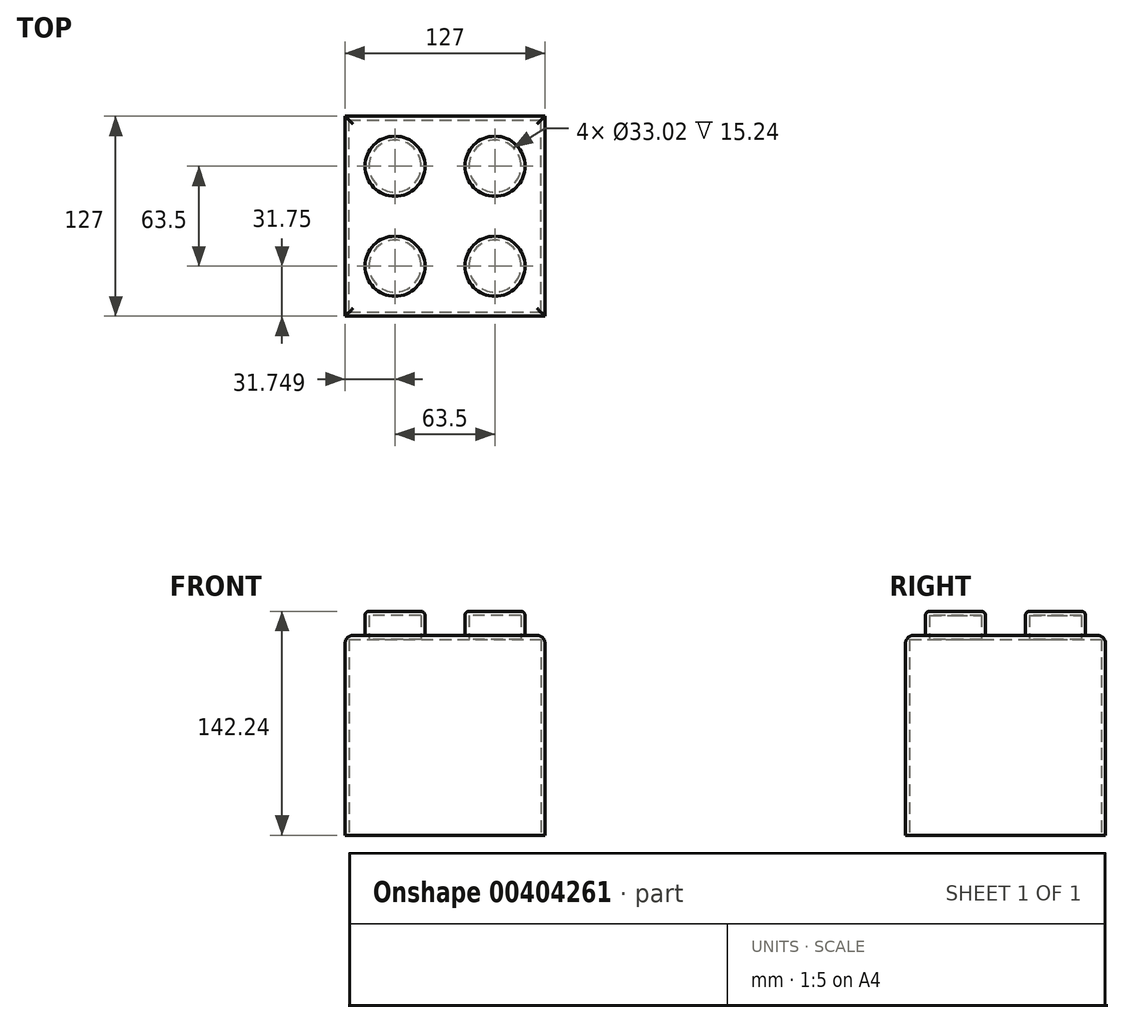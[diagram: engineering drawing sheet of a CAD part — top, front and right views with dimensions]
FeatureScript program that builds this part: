
annotation { "Feature Type Name" : "Feature", "Feature Type Description" : "" }
export const myFeature = defineFeature(function(context is Context, id is Id, definition is map)
    precondition{}
    {
        {
            var Q0;
            Q0=qCreatedBy(makeId("Front.planeOp"),FACE);
            var sketch = newSketch(context, id + "F0", { "sketchPlane" : qUnion([Q0])});
            skLineSegment(sketch, "E0.bottom", {"start": v(-58.78, 63.4) * mm, "end": v(68.22, 63.4) * mm});
            skLineSegment(sketch, "E0.top", {"start": v(-58.78, -63.6) * mm, "end": v(68.22, -63.6) * mm});
            skLineSegment(sketch, "E0.left", {"start": v(-58.78, 63.4) * mm, "end": v(-58.78, -63.6) * mm});
            skLineSegment(sketch, "E0.right", {"start": v(68.22, 63.4) * mm, "end": v(68.22, -63.6) * mm});
            skSolve(sketch);
        }
        {
            var Q0;
            Q0=makeQuery(id+"F0.imprint","IMPRINT",FACE,{"disambiguationData":[TD([[makeQuery(id+"F0.imprint","IMPRINT",EDGE,{"derivedFrom":sQuery(id+"F0.wireOp",EDGE,"E0.bottom")}),-1.0]])]});
            extrude(context, id + "F1", {"entities" : qUnion([Q0]), "depth" : 127 * mm});
        }
        {
            var Q0;
            Q0=makeQuery(id+"F1.opExtrude","SWEPT_FACE",FACE,{"disambiguationData":[OSD([sQuery(id+"F0.wireOp",EDGE,"E0.bottom")])]});
            var sketch = newSketch(context, id + "F2", { "sketchPlane" : qUnion([Q0])});
            skCircle(sketch, "E1", {"center": v(-27.03, -95.25) * mm, "radius": 19.05 * mm});
            skCircle(sketch, "E2", {"center": v(36.47, -95.25) * mm, "radius": 19.05 * mm});
            skCircle(sketch, "E3", {"center": v(36.47, -31.75) * mm, "radius": 19.05 * mm});
            skCircle(sketch, "E4", {"center": v(-27.03, -31.75) * mm, "radius": 19.05 * mm});
            skSolve(sketch);
        }
        {
            var Q0;
            Q0=makeQuery(id+"F2.imprint","IMPRINT",FACE,{"disambiguationData":[TD([[makeQuery(id+"F2.imprint","IMPRINT",EDGE,{"derivedFrom":sQuery(id+"F2.wireOp",EDGE,"E1")}),1.0]])]});
            var Q1;
            Q1=makeQuery(id+"F2.imprint","IMPRINT",FACE,{"disambiguationData":[TD([[makeQuery(id+"F2.imprint","IMPRINT",EDGE,{"derivedFrom":sQuery(id+"F2.wireOp",EDGE,"E4")}),1.0]])]});
            var Q2;
            Q2=makeQuery(id+"F2.imprint","IMPRINT",FACE,{"disambiguationData":[TD([[makeQuery(id+"F2.imprint","IMPRINT",EDGE,{"derivedFrom":sQuery(id+"F2.wireOp",EDGE,"E3")}),1.0]])]});
            var Q3;
            Q3=makeQuery(id+"F2.imprint","IMPRINT",FACE,{"disambiguationData":[TD([[makeQuery(id+"F2.imprint","IMPRINT",EDGE,{"derivedFrom":sQuery(id+"F2.wireOp",EDGE,"E2")}),1.0]])]});
            extrude(context, id + "F3", {"entities" : qUnion([Q0, Q1, Q2, Q3]), "operationType" : NewBodyOperationType.ADD, "depth" : 15.24 * mm});
        }
        {
            var Q0;
            Q0=makeQuery(id+"F3.opExtrude","CAP_EDGE",EDGE,{"disambiguationData":[OSD([sQuery(id+"F2.wireOp",EDGE,"E1")])],"isStart":false});
            var Q1;
            Q1=makeQuery(id+"F3.opExtrude","CAP_EDGE",EDGE,{"disambiguationData":[OSD([sQuery(id+"F2.wireOp",EDGE,"E4")])],"isStart":false});
            var Q2;
            Q2=makeQuery(id+"F3.opExtrude","CAP_EDGE",EDGE,{"disambiguationData":[OSD([sQuery(id+"F2.wireOp",EDGE,"E3")])],"isStart":false});
            var Q3;
            Q3=makeQuery(id+"F3.opExtrude","CAP_FACE",FACE,{"disambiguationData":[OSD([sQuery(id+"F2.wireOp",EDGE,"E2")])],"isStart":false});
            fillet(context, id + "F4", {"entities" : qUnion([Q0, Q1, Q2, Q3]), "radius" : 2.54 * mm, "tangentPropagation" : true, "allowEdgeOverflow" : false});
        }
        {
            var Q0;
            Q0=makeQuery(id+"F1.opExtrude","SWEPT_FACE",FACE,{"disambiguationData":[OSD([sQuery(id+"F0.wireOp",EDGE,"E0.top")])]});
            shell(context, id + "F5", {"entities" : qUnion([Q0]), "thickness" : 2.54 * mm});
        }
        {
            var Q0;
            Q0=makeQuery(id+"F1.opExtrude","CAP_EDGE",EDGE,{"disambiguationData":[OSD([sQuery(id+"F0.wireOp",EDGE,"E0.bottom")])],"isStart":false});
            var Q1;
            Q1=makeQuery(id+"F1.opExtrude","SWEPT_EDGE",EDGE,{"disambiguationData":[OSD([sQuery(id+"F0.wireOp",EDGE,"E0.bottom"),sQuery(id+"F0.wireOp",EDGE,"E0.left")])]});
            var Q2;
            Q2=makeQuery(id+"F1.opExtrude","CAP_EDGE",EDGE,{"disambiguationData":[OSD([sQuery(id+"F0.wireOp",EDGE,"E0.bottom")])],"isStart":true});
            var Q3;
            Q3=makeQuery(id+"F1.opExtrude","SWEPT_EDGE",EDGE,{"disambiguationData":[OSD([sQuery(id+"F0.wireOp",EDGE,"E0.bottom"),sQuery(id+"F0.wireOp",EDGE,"E0.right")])]});
            fillet(context, id + "F6", {"entities" : qUnion([Q0, Q1, Q2, Q3]), "radius" : 5.08 * mm, "tangentPropagation" : true, "allowEdgeOverflow" : false});
        }
    });
